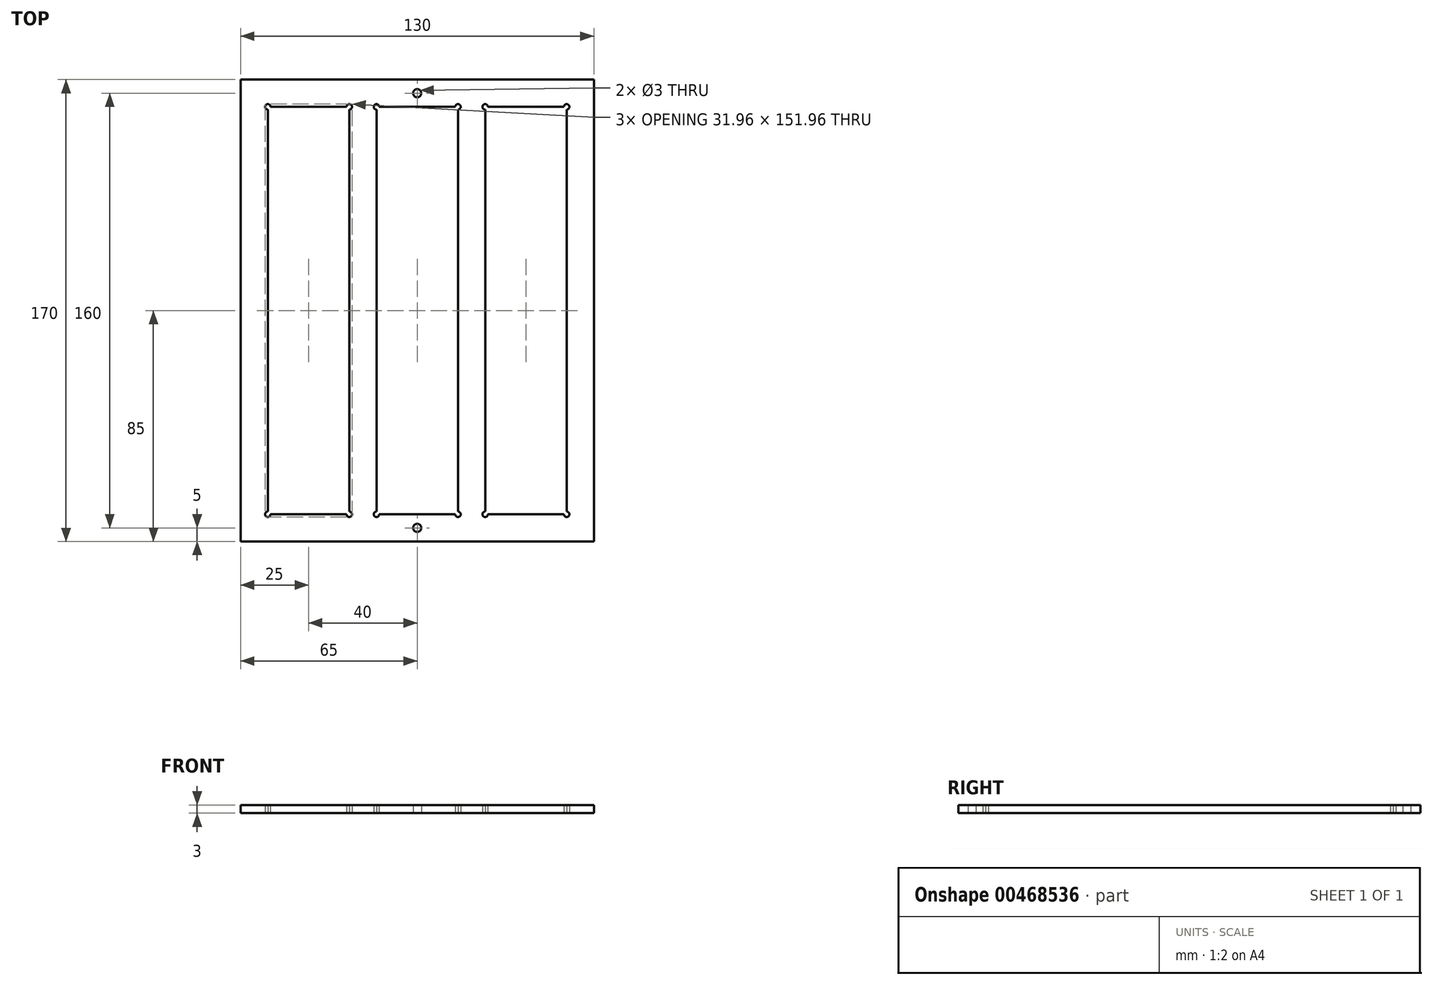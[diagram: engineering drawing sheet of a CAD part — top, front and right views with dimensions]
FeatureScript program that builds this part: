
annotation { "Feature Type Name" : "Feature", "Feature Type Description" : "" }
export const myFeature = defineFeature(function(context is Context, id is Id, definition is map)
    precondition{}
    {
        {
            var Q0;
            Q0=qCreatedBy(makeId("Top.planeOp"),FACE);
            var sketch = newSketch(context, id + "F0", { "sketchPlane" : qUnion([Q0])});
            skLineSegment(sketch, "E0.bottom", {"start": v(-65, 85) * mm, "end": v(65, 85) * mm});
            skLineSegment(sketch, "E0.top", {"start": v(-65, -85) * mm, "end": v(65, -85) * mm});
            skLineSegment(sketch, "E0.left", {"start": v(-65, 85) * mm, "end": v(-65, -85) * mm});
            skLineSegment(sketch, "E0.right", {"start": v(65, 85) * mm, "end": v(65, -85) * mm});
            skPoint(sketch, "E1", {"position": v(0, 85) * mm});
            skPoint(sketch, "E2", {"position": v(-65, 0) * mm});
            skLineSegment(sketch, "E3", {"start": v(-55, 85) * mm, "end": v(-55, -85) * mm, "construction": true});
            skLineSegment(sketch, "E4", {"start": v(-15, 85) * mm, "end": v(-15, -85) * mm, "construction": true});
            skLineSegment(sketch, "E5", {"start": v(25, 85) * mm, "end": v(25, -85) * mm, "construction": true});
            skLineSegment(sketch, "E6", {"start": v(-65, 75) * mm, "end": v(65, 75) * mm, "construction": true});
            skLineSegment(sketch, "E7.bottom", {"start": v(-55, 75) * mm, "end": v(-25, 75) * mm});
            skLineSegment(sketch, "E7.top", {"start": v(-55, -75) * mm, "end": v(-25, -75) * mm});
            skLineSegment(sketch, "E7.left", {"start": v(-55, 75) * mm, "end": v(-55, -75) * mm});
            skLineSegment(sketch, "E7.right", {"start": v(-25, 75) * mm, "end": v(-25, -75) * mm});
            skLineSegment(sketch, "E8.bottom", {"start": v(-15, 75) * mm, "end": v(15, 75) * mm});
            skLineSegment(sketch, "E8.top", {"start": v(-15, -75) * mm, "end": v(15, -75) * mm});
            skLineSegment(sketch, "E8.left", {"start": v(-15, 75) * mm, "end": v(-15, -75) * mm});
            skLineSegment(sketch, "E8.right", {"start": v(15, 75) * mm, "end": v(15, -75) * mm});
            skLineSegment(sketch, "E9.bottom", {"start": v(25, 75) * mm, "end": v(55, 75) * mm});
            skLineSegment(sketch, "E9.top", {"start": v(25, -75) * mm, "end": v(55, -75) * mm});
            skLineSegment(sketch, "E9.left", {"start": v(25, 75) * mm, "end": v(25, -75) * mm});
            skLineSegment(sketch, "E9.right", {"start": v(55, 75) * mm, "end": v(55, -75) * mm});
            skCircle(sketch, "E10", {"center": v(-55, 75) * mm, "radius": 1 * mm});
            skCircle(sketch, "E11", {"center": v(-25, 75) * mm, "radius": 1 * mm});
            skCircle(sketch, "E12", {"center": v(-15, 75) * mm, "radius": 1 * mm});
            skCircle(sketch, "E13", {"center": v(15, 75) * mm, "radius": 1 * mm});
            skCircle(sketch, "E14", {"center": v(55, 75) * mm, "radius": 1 * mm});
            skCircle(sketch, "E15", {"center": v(25, 75) * mm, "radius": 1 * mm});
            skCircle(sketch, "E16", {"center": v(-55, -75) * mm, "radius": 1 * mm});
            skCircle(sketch, "E17", {"center": v(-25, -75) * mm, "radius": 1 * mm});
            skCircle(sketch, "E18", {"center": v(-15, -75) * mm, "radius": 1 * mm});
            skCircle(sketch, "E19", {"center": v(15, -75) * mm, "radius": 1 * mm});
            skCircle(sketch, "E20", {"center": v(25, -75) * mm, "radius": 1 * mm});
            skCircle(sketch, "E21", {"center": v(55, -75) * mm, "radius": 1 * mm});
            skLineSegment(sketch, "E22", {"start": v(0, 85) * mm, "end": v(0, 75) * mm, "construction": true});
            skCircle(sketch, "E23", {"center": v(0, 80) * mm, "radius": 1.5 * mm});
            skLineSegment(sketch, "E24", {"start": v(0, -85) * mm, "end": v(0, -75) * mm, "construction": true});
            skCircle(sketch, "E25", {"center": v(0, -80) * mm, "radius": 1.5 * mm});
            skSolve(sketch);
        }
        {
            var Q0;
            Q0 = qSketchRegion(id + "F0", true);
            var Q1;
            Q1=makeQuery(id+"F0.imprint","IMPRINT",FACE,{"disambiguationData":[TD([[makeQuery(id+"F0.imprint","IMPRINT",EDGE,{"derivedFrom":sQuery(id+"F0.wireOp",EDGE,"E0.bottom")}),-1.0]])]});
            extrude(context, id + "F1", {"entities" : qUnion([Q0, Q1]), "depth" : 3 * mm, "offsetDistance" : 25 * mm});
        }
    });
